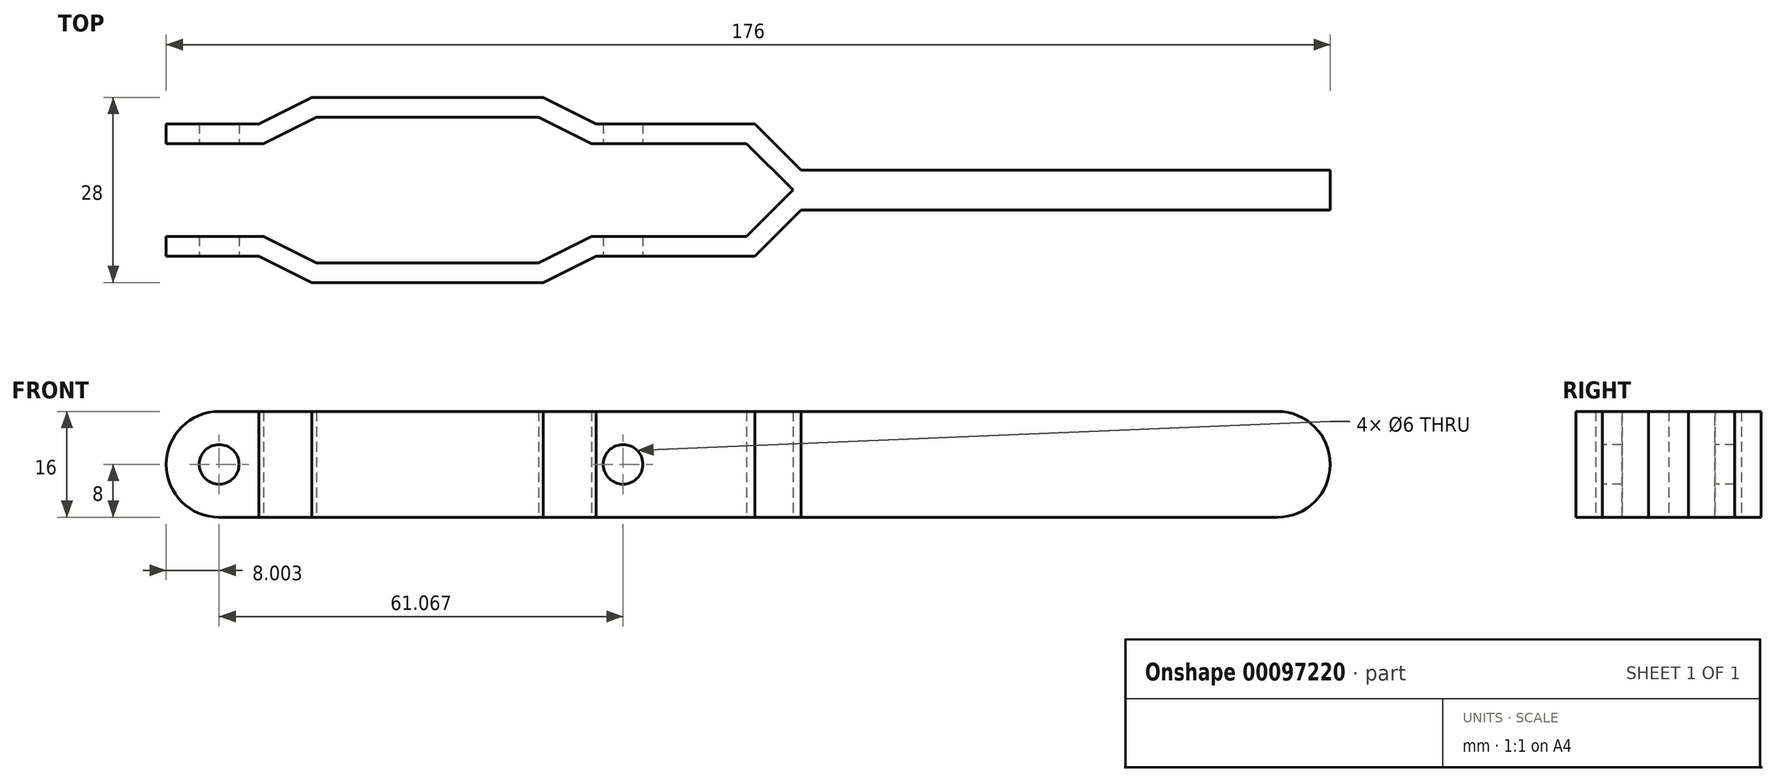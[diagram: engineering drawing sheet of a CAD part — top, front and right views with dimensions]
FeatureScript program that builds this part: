
annotation { "Feature Type Name" : "Feature", "Feature Type Description" : "" }
export const myFeature = defineFeature(function(context is Context, id is Id, definition is map)
    precondition{}
    {
        {
            var Q0;
            Q0=qCreatedBy(makeId("Top.planeOp"),FACE);
            var sketch = newSketch(context, id + "F0", { "sketchPlane" : qUnion([Q0])});
            skLineSegment(sketch, "E0", {"start": v(-86.76, 10) * mm, "end": v(-80.76, 10) * mm});
            skLineSegment(sketch, "E1", {"start": v(-80.76, 10) * mm, "end": v(-72.76, 14) * mm});
            skLineSegment(sketch, "E2", {"start": v(-72.76, 14) * mm, "end": v(-37.76, 14) * mm});
            skLineSegment(sketch, "E3", {"start": v(-37.76, 14) * mm, "end": v(-29.76, 10) * mm});
            skLineSegment(sketch, "E4", {"start": v(-29.76, 10) * mm, "end": v(-5.76, 10) * mm});
            skLineSegment(sketch, "E5", {"start": v(-5.76, 10) * mm, "end": v(1.24, 3) * mm});
            skLineSegment(sketch, "E6", {"start": v(1.24, 3) * mm, "end": v(73.24, 3) * mm});
            skLineSegment(sketch, "E7.1", {"start": v(-7, 7) * mm, "end": v(0, 0) * mm});
            skLineSegment(sketch, "E7.2", {"start": v(-30.47, 7) * mm, "end": v(-7, 7) * mm});
            skLineSegment(sketch, "E7.3", {"start": v(-86.76, 7) * mm, "end": v(-80.05, 7) * mm});
            skLineSegment(sketch, "E7.4", {"start": v(-80.05, 7) * mm, "end": v(-72.05, 11) * mm});
            skLineSegment(sketch, "E7.5", {"start": v(-72.05, 11) * mm, "end": v(-38.47, 11) * mm});
            skLineSegment(sketch, "E7.6", {"start": v(-38.47, 11) * mm, "end": v(-30.47, 7) * mm});
            skLineSegment(sketch, "E8", {"start": v(-86.76, 10) * mm, "end": v(-86.76, 7) * mm});
            skLineSegment(sketch, "E9.MirrorCS", {"start": v(-86.76, -7) * mm, "end": v(-80.05, -7) * mm});
            skLineSegment(sketch, "E10.MirrorCS", {"start": v(-86.76, -10) * mm, "end": v(-86.76, -7) * mm});
            skLineSegment(sketch, "E11.MirrorCS", {"start": v(-86.76, -10) * mm, "end": v(-80.76, -10) * mm});
            skLineSegment(sketch, "E12.MirrorCS", {"start": v(-80.76, -10) * mm, "end": v(-72.76, -14) * mm});
            skLineSegment(sketch, "E13.MirrorCS", {"start": v(-80.05, -7) * mm, "end": v(-72.05, -11) * mm});
            skLineSegment(sketch, "E14.MirrorCS", {"start": v(-72.05, -11) * mm, "end": v(-38.47, -11) * mm});
            skLineSegment(sketch, "E15.MirrorCS", {"start": v(-72.76, -14) * mm, "end": v(-37.76, -14) * mm});
            skLineSegment(sketch, "E16.MirrorCS", {"start": v(-38.47, -11) * mm, "end": v(-30.47, -7) * mm});
            skLineSegment(sketch, "E17.MirrorCS", {"start": v(-37.76, -14) * mm, "end": v(-29.76, -10) * mm});
            skLineSegment(sketch, "E18.MirrorCS", {"start": v(-30.47, -7) * mm, "end": v(-7, -7) * mm});
            skLineSegment(sketch, "E19.MirrorCS", {"start": v(-29.76, -10) * mm, "end": v(-5.76, -10) * mm});
            skLineSegment(sketch, "E20.MirrorCS", {"start": v(-7, -7) * mm, "end": v(0, 0) * mm});
            skLineSegment(sketch, "E21.MirrorCS", {"start": v(-5.76, -10) * mm, "end": v(1.24, -3) * mm});
            skLineSegment(sketch, "E22.MirrorCS", {"start": v(1.24, -3) * mm, "end": v(73.24, -3) * mm});
            skLineSegment(sketch, "E23", {"start": v(73.24, 3) * mm, "end": v(73.24, -3) * mm});
            skSolve(sketch);
        }
        {
            var Q0;
            Q0 = qSketchRegion(id + "F0", true);
            extrude(context, id + "F1", {"entities" : qUnion([Q0]), "depth" : 16 * mm});
        }
        {
            var Q0;
            Q0=makeQuery(id+"F1.opExtrude","SWEPT_FACE",FACE,{"disambiguationData":[OSD([sQuery(id+"F0.wireOp",EDGE,"E11.MirrorCS")])]});
            var sketch = newSketch(context, id + "F2", { "sketchPlane" : qUnion([Q0])});
            skLineSegment(sketch, "E24", {"start": v(-86.76, 8) * mm, "end": v(-6.13, 8) * mm, "construction": true});
            skPoint(sketch, "E24.endSnap0", {"position": v(-80.76, 8) * mm});
            skArc(sketch, "E25.0.startCap", {"start": v(-86.76, 0) * mm, "mid": v(-94.76, 8) * mm, "end": v(-86.76, 16) * mm, "construction": true});
            skArc(sketch, "E25.0.endCap", {"start": v(-6.13, 16) * mm, "mid": v(1.87, 8) * mm, "end": v(-6.13, 0) * mm, "construction": true});
            skLineSegment(sketch, "E25.0.left", {"start": v(-86.76, 16) * mm, "end": v(-6.13, 16) * mm, "construction": true});
            skLineSegment(sketch, "E25.0.right", {"start": v(-86.76, 0) * mm, "end": v(-6.13, 0) * mm, "construction": true});
            skCircle(sketch, "E26", {"center": v(-86.76, 8) * mm, "radius": 3 * mm});
            skCircle(sketch, "E27", {"center": v(-25.7, 8) * mm, "radius": 3 * mm});
            skSolve(sketch);
        }
        {
            var Q0;
            {var subQ0=sQuery(id+"F0.wireOp",EDGE,"E0");var subQ1=sQuery(id+"F0.wireOp",EDGE,"E8");var subQ2=sQuery(id+"F0.wireOp",EDGE,"E7.3");Q0=makeQuery(id+"F7.hole-0.boolean.opBoolean","SPLIT",FACE,{"disambiguationData":[TD([makeQuery(id+"F1.opExtrude","CAP_FACE",FACE,{"disambiguationData":[OSD([subQ0,sQuery(id+"F0.wireOp",EDGE,"E1"),sQuery(id+"F0.wireOp",EDGE,"E2"),sQuery(id+"F0.wireOp",EDGE,"E3"),sQuery(id+"F0.wireOp",EDGE,"E4"),sQuery(id+"F0.wireOp",EDGE,"E5"),sQuery(id+"F0.wireOp",EDGE,"E6"),sQuery(id+"F0.wireOp",EDGE,"E7.1"),sQuery(id+"F0.wireOp",EDGE,"E7.2"),subQ2,sQuery(id+"F0.wireOp",EDGE,"E7.4"),sQuery(id+"F0.wireOp",EDGE,"E7.5"),sQuery(id+"F0.wireOp",EDGE,"E7.6"),subQ1,sQuery(id+"F0.wireOp",EDGE,"E9.MirrorCS"),sQuery(id+"F0.wireOp",EDGE,"E10.MirrorCS"),sQuery(id+"F0.wireOp",EDGE,"E11.MirrorCS"),sQuery(id+"F0.wireOp",EDGE,"E12.MirrorCS"),sQuery(id+"F0.wireOp",EDGE,"E13.MirrorCS"),sQuery(id+"F0.wireOp",EDGE,"E14.MirrorCS"),sQuery(id+"F0.wireOp",EDGE,"E15.MirrorCS"),sQuery(id+"F0.wireOp",EDGE,"E16.MirrorCS"),sQuery(id+"F0.wireOp",EDGE,"E17.MirrorCS"),sQuery(id+"F0.wireOp",EDGE,"E18.MirrorCS"),sQuery(id+"F0.wireOp",EDGE,"E19.MirrorCS"),sQuery(id+"F0.wireOp",EDGE,"E20.MirrorCS"),sQuery(id+"F0.wireOp",EDGE,"E21.MirrorCS"),sQuery(id+"F0.wireOp",EDGE,"E22.MirrorCS"),sQuery(id+"F0.wireOp",EDGE,"E23")])],"isStart":false})])],"derivedFrom":makeQuery(id+"F1.opExtrude","SWEPT_FACE",FACE,{"disambiguationData":[OSD([subQ1])]})});}
            var sketch = newSketch(context, id + "F3", { "sketchPlane" : qUnion([Q0])});
            skLineSegment(sketch, "E28", {"start": v(-10, 16) * mm, "end": v(-7, 16) * mm});
            skLineSegment(sketch, "E29", {"start": v(-10, 16) * mm, "end": v(-10, 0) * mm});
            skLineSegment(sketch, "E30", {"start": v(-10, 0) * mm, "end": v(-7, 0) * mm});
            skLineSegment(sketch, "E31", {"start": v(-7, 0) * mm, "end": v(-7, 16) * mm});
            skLineSegment(sketch, "E32.MirrorCS", {"start": v(7, 0) * mm, "end": v(7, 16) * mm});
            skLineSegment(sketch, "E33.MirrorCS", {"start": v(10, 16) * mm, "end": v(10, 0) * mm});
            skLineSegment(sketch, "E34.MirrorCS", {"start": v(10, 16) * mm, "end": v(7, 16) * mm});
            skLineSegment(sketch, "E35.MirrorCS", {"start": v(10, 0) * mm, "end": v(7, 0) * mm});
            skSolve(sketch);
        }
        {
            var Q0;
            Q0=makeQuery(id+"F1.opExtrude","SWEPT_FACE",FACE,{"disambiguationData":[OSD([sQuery(id+"F0.wireOp",EDGE,"E23")])]});
            var sketch = newSketch(context, id + "F4", { "sketchPlane" : qUnion([Q0])});
            skLineSegment(sketch, "E36", {"start": v(-3, 16) * mm, "end": v(3, 16) * mm});
            skLineSegment(sketch, "E37", {"start": v(3, 16) * mm, "end": v(3, 0) * mm});
            skLineSegment(sketch, "E38", {"start": v(3, 0) * mm, "end": v(-3, 0) * mm});
            skLineSegment(sketch, "E39", {"start": v(-3, 0) * mm, "end": v(-3, 16) * mm});
            skSolve(sketch);
        }
        {
            var Q0;
            Q0 = qSketchRegion(id + "F3", true);
            extrude(context, id + "F5", {"entities" : qUnion([Q0]), "operationType" : NewBodyOperationType.ADD, "depth" : 8 * mm});
        }
        {
            var Q0;
            Q0 = qSketchRegion(id + "F4", true);
            extrude(context, id + "F6", {"entities" : qUnion([Q0]), "operationType" : NewBodyOperationType.ADD, "depth" : 8 * mm});
        }
        {
            var Q0;
            Q0=sQuery(id+"F2.wireOp",VERTEX,"E26.center");
            var Q1;
            Q1=sQuery(id+"F2.wireOp",VERTEX,"E27.center");
            var Q2;
            Q2=makeQuery(id+"F1.opExtrude","SWEPT_BODY",BODY,{"disambiguationData":[OSD([sQuery(id+"F0.wireOp",EDGE,"E0"),sQuery(id+"F0.wireOp",EDGE,"E1"),sQuery(id+"F0.wireOp",EDGE,"E2"),sQuery(id+"F0.wireOp",EDGE,"E3"),sQuery(id+"F0.wireOp",EDGE,"E4"),sQuery(id+"F0.wireOp",EDGE,"E5"),sQuery(id+"F0.wireOp",EDGE,"E6"),sQuery(id+"F0.wireOp",EDGE,"E7.1"),sQuery(id+"F0.wireOp",EDGE,"E7.2"),sQuery(id+"F0.wireOp",EDGE,"E7.3"),sQuery(id+"F0.wireOp",EDGE,"E7.4"),sQuery(id+"F0.wireOp",EDGE,"E7.5"),sQuery(id+"F0.wireOp",EDGE,"E7.6"),sQuery(id+"F0.wireOp",EDGE,"E8"),sQuery(id+"F0.wireOp",EDGE,"E9.MirrorCS"),sQuery(id+"F0.wireOp",EDGE,"E10.MirrorCS"),sQuery(id+"F0.wireOp",EDGE,"E11.MirrorCS"),sQuery(id+"F0.wireOp",EDGE,"E12.MirrorCS"),sQuery(id+"F0.wireOp",EDGE,"E13.MirrorCS"),sQuery(id+"F0.wireOp",EDGE,"E14.MirrorCS"),sQuery(id+"F0.wireOp",EDGE,"E15.MirrorCS"),sQuery(id+"F0.wireOp",EDGE,"E16.MirrorCS"),sQuery(id+"F0.wireOp",EDGE,"E17.MirrorCS"),sQuery(id+"F0.wireOp",EDGE,"E18.MirrorCS"),sQuery(id+"F0.wireOp",EDGE,"E19.MirrorCS"),sQuery(id+"F0.wireOp",EDGE,"E20.MirrorCS"),sQuery(id+"F0.wireOp",EDGE,"E21.MirrorCS"),sQuery(id+"F0.wireOp",EDGE,"E22.MirrorCS"),sQuery(id+"F0.wireOp",EDGE,"E23")])]});
            hole(context, id + "F7", {"style" : HoleStyle.SIMPLE, "endStyle" : HoleEndStyle.THROUGH, "holeDiameter" : 6 * mm, "locations" : qUnion([Q0, Q1]), "scope" : qUnion([Q2]), "isTappedThrough" : true});
        }
        {
            var Q0;
            Q0=makeQuery(id+"F5.opExtrude","CAP_EDGE",EDGE,{"disambiguationData":[OSD([sQuery(id+"F3.wireOp",EDGE,"E34.MirrorCS")])],"isStart":false});
            var Q1;
            Q1=makeQuery(id+"F5.opExtrude","CAP_EDGE",EDGE,{"disambiguationData":[OSD([sQuery(id+"F3.wireOp",EDGE,"E35.MirrorCS")])],"isStart":false});
            var Q2;
            Q2=makeQuery(id+"F5.opExtrude","CAP_EDGE",EDGE,{"disambiguationData":[OSD([sQuery(id+"F3.wireOp",EDGE,"E30")])],"isStart":false});
            var Q3;
            Q3=makeQuery(id+"F5.opExtrude","CAP_EDGE",EDGE,{"disambiguationData":[OSD([sQuery(id+"F3.wireOp",EDGE,"E28")])],"isStart":false});
            var Q4;
            Q4=makeQuery(id+"F6.opExtrude","CAP_EDGE",EDGE,{"disambiguationData":[OSD([sQuery(id+"F4.wireOp",EDGE,"E36")])],"isStart":false});
            var Q5;
            Q5=makeQuery(id+"F6.opExtrude","CAP_EDGE",EDGE,{"disambiguationData":[OSD([sQuery(id+"F4.wireOp",EDGE,"E38")])],"isStart":false});
            fillet(context, id + "F8", {"entities" : qUnion([Q0, Q1, Q2, Q3, Q4, Q5]), "radius" : 8 * mm, "tangentPropagation" : true, "allowEdgeOverflow" : false});
        }
    });
